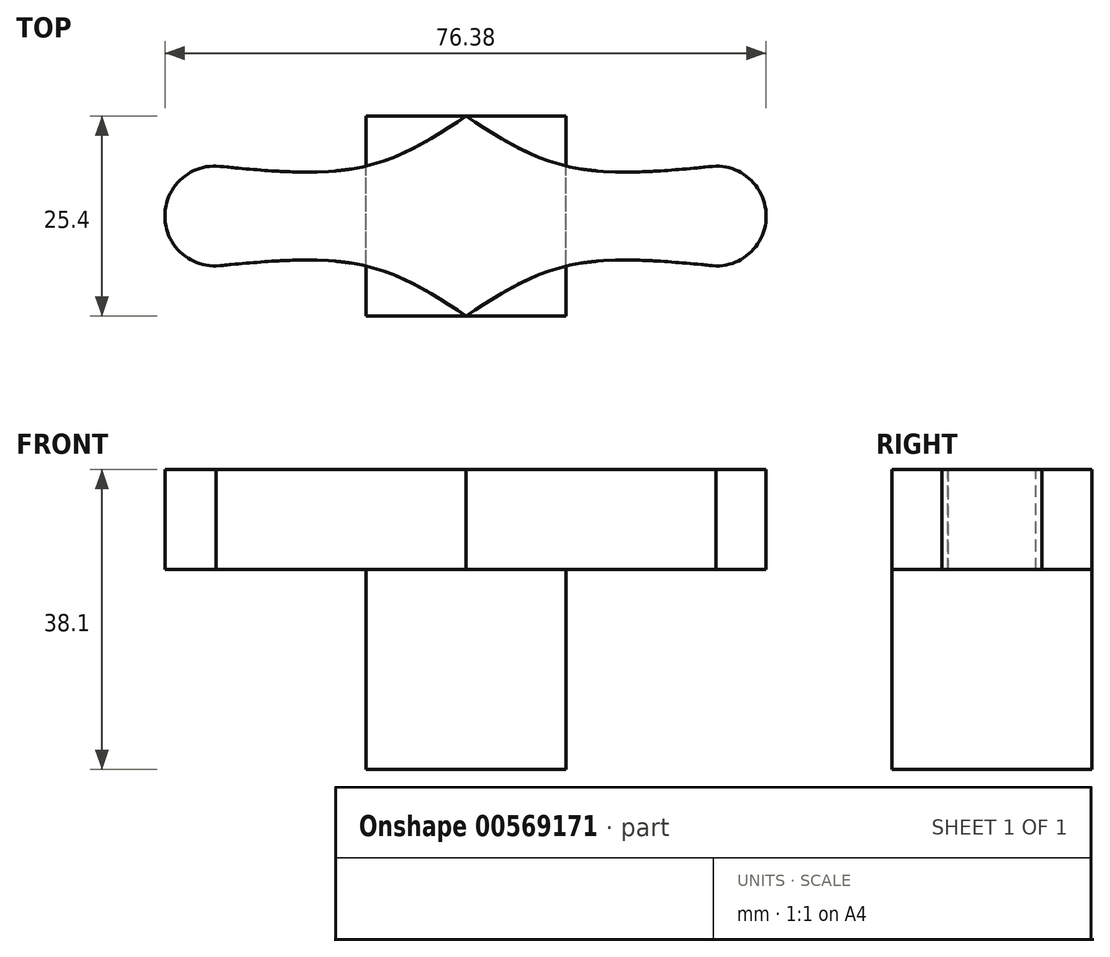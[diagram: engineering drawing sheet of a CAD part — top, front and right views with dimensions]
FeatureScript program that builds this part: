
annotation { "Feature Type Name" : "Feature", "Feature Type Description" : "" }
export const myFeature = defineFeature(function(context is Context, id is Id, definition is map)
    precondition{}
    {
        {
            var Q0;
            Q0=qCreatedBy(makeId("Front.planeOp"),FACE);
            var sketch = newSketch(context, id + "F0", { "sketchPlane" : qUnion([Q0])});
            skLineSegment(sketch, "E0", {"start": v(-11.6, 26.96) * mm, "end": v(-11.6, -11.14) * mm});
            skLineSegment(sketch, "E1", {"start": v(-11.6, -11.14) * mm, "end": v(13.8, -11.14) * mm});
            skLineSegment(sketch, "E2", {"start": v(13.8, -11.14) * mm, "end": v(13.8, 26.96) * mm});
            skLineSegment(sketch, "E3", {"start": v(13.8, 26.96) * mm, "end": v(-11.6, 26.96) * mm});
            skSolve(sketch);
        }
        {
            var Q0;
            Q0=makeQuery(id+"F0.imprint","IMPRINT",FACE,{"disambiguationData":[TD([[makeQuery(id+"F0.imprint","IMPRINT",EDGE,{"derivedFrom":sQuery(id+"F0.wireOp",EDGE,"E0")}),1.0]])]});
            extrude(context, id + "F1", {"entities" : qUnion([Q0]), "depth" : 25.4 * mm, "offsetDistance" : 25.4 * mm});
        }
        {
            var Q0;
            Q0=makeQuery(id+"F1.opExtrude","SWEPT_FACE",FACE,{"disambiguationData":[OSD([sQuery(id+"F0.wireOp",EDGE,"E3")])]});
            var sketch = newSketch(context, id + "F2", { "sketchPlane" : qUnion([Q0])});
            skLineSegment(sketch, "E4", {"start": v(-11.6, -25.4) * mm, "end": v(-11.6, -19.05) * mm});
            skLineSegment(sketch, "E5", {"start": v(-11.6, 0) * mm, "end": v(-11.6, -6.35) * mm});
            skLineSegment(sketch, "E6", {"start": v(13.8, 0) * mm, "end": v(13.8, -6.35) * mm});
            skLineSegment(sketch, "E7", {"start": v(13.8, -6.35) * mm, "end": v(32.85, -6.35) * mm});
            skLineSegment(sketch, "E8", {"start": v(13.8, -25.4) * mm, "end": v(13.8, -19.05) * mm});
            skLineSegment(sketch, "E9", {"start": v(13.8, -19.05) * mm, "end": v(32.86, -19.05) * mm});
            skLineSegment(sketch, "E10", {"start": v(32.86, -19.05) * mm, "end": v(32.85, -6.35) * mm});
            skLineSegment(sketch, "E11", {"start": v(-11.6, -19.05) * mm, "end": v(-30.65, -19.05) * mm});
            skLineSegment(sketch, "E12", {"start": v(-30.65, -19.05) * mm, "end": v(-30.65, -6.35) * mm});
            skLineSegment(sketch, "E13", {"start": v(-30.65, -6.35) * mm, "end": v(-11.6, -6.35) * mm});
            skSolve(sketch);
        }
        {
            var Q0;
            {var subQ0=sQuery(id+"F2.wireOp",EDGE,"E11");Q0=makeQuery(id+"F2.imprint","IMPRINT",FACE,{"disambiguationData":[TD([[makeQuery(id+"F2.imprint","IMPRINT",EDGE,{"derivedFrom":subQ0}),-1.0]])]});}
            var Q1;
            {var subQ0=sQuery(id+"F2.wireOp",EDGE,"E7");Q1=makeQuery(id+"F2.imprint","IMPRINT",FACE,{"disambiguationData":[TD([[makeQuery(id+"F2.imprint","IMPRINT",EDGE,{"derivedFrom":subQ0}),-1.0]])]});}
            extrude(context, id + "F3", {"entities" : qUnion([Q0, Q1]), "operationType" : NewBodyOperationType.ADD, "depth" : -12.7 * mm, "offsetDistance" : 25.4 * mm});
        }
        {
            var Q0;
            {var subQ0=sQuery(id+"F0.wireOp",EDGE,"E3");Q0=makeQuery(id+"F3.boolean.opBoolean","MERGE",FACE,{"derivedFrom":[makeQuery(id+"F1.opExtrude","SWEPT_FACE",FACE,{"disambiguationData":[OSD([subQ0])]}),makeQuery(id+"F3.opExtrude","CAP_FACE",FACE,{"disambiguationData":[OSD([sQuery(id+"F0.wireOp",EDGE,"E2"),subQ0,sQuery(id+"F2.wireOp",EDGE,"E7"),sQuery(id+"F2.wireOp",EDGE,"E9"),sQuery(id+"F2.wireOp",EDGE,"E10")])],"isStart":true}),makeQuery(id+"F3.opExtrude","CAP_FACE",FACE,{"disambiguationData":[OSD([sQuery(id+"F0.wireOp",EDGE,"E0"),subQ0,sQuery(id+"F2.wireOp",EDGE,"E11"),sQuery(id+"F2.wireOp",EDGE,"E12"),sQuery(id+"F2.wireOp",EDGE,"E13")])],"isStart":true})]});}
            var sketch = newSketch(context, id + "F4", { "sketchPlane" : qUnion([Q0])});
            skLineSegment(sketch, "E14", {"start": v(-11.6, -25.4) * mm, "end": v(1.1, -25.4) * mm});
            skFitSpline(sketch, "E15", {"points": [v(1.1, -25.4) * mm, v(-11.6, -19.05) * mm, v(-30.65, -19.05) * mm], "startDerivative": vector(-25.54, 16.88) * mm, "endDerivative": vector(-37.67, -3.68) * mm});
            skLineSegment(sketch, "E16", {"start": v(-11.6, 0) * mm, "end": v(1.1, 0) * mm});
            skFitSpline(sketch, "E17", {"points": [v(1.1, 0) * mm, v(-11.6, -6.35) * mm, v(-30.65, -6.35) * mm], "startDerivative": vector(-25.54, -16.88) * mm, "endDerivative": vector(-37.67, 3.68) * mm});
            skFitSpline(sketch, "E18", {"points": [v(1.1, 0) * mm, v(13.8, -6.35) * mm, v(32.85, -6.35) * mm], "startDerivative": vector(25.54, -16.88) * mm, "endDerivative": vector(37.67, 3.68) * mm});
            skFitSpline(sketch, "E19", {"points": [v(1.1, -25.4) * mm, v(13.8, -19.05) * mm, v(32.86, -19.05) * mm], "startDerivative": vector(25.54, 16.88) * mm, "endDerivative": vector(37.68, -3.68) * mm});
            skSolve(sketch);
        }
        {
            var Q0;
            {var subQ0=sQuery(id+"F4.wireOp",EDGE,"E14");Q0=makeQuery(id+"F4.imprint","IMPRINT",FACE,{"disambiguationData":[TD([[makeQuery(id+"F4.imprint","IMPRINT",EDGE,{"derivedFrom":subQ0}),-1.0]])]});}
            var Q1;
            {var subQ1=sQuery(id+"F2.wireOp",EDGE,"E9");var subQ2=sQuery(id+"F0.wireOp",EDGE,"E3");var subQ3=sQuery(id+"F0.wireOp",EDGE,"E2");var subQ5=makeQuery(id+"F3.boolean.opBoolean","SPLIT",EDGE,{"disambiguationData":[TD([makeQuery(id+"F3.opExtrude","SWEPT_FACE",FACE,{"disambiguationData":[OSD([subQ1])]})])],"derivedFrom":makeQuery(id+"F1.opExtrude","SWEPT_EDGE",EDGE,{"disambiguationData":[OSD([subQ3,subQ2])]})});Q1=makeQuery(id+"F4.imprint","IMPRINT",FACE,{"disambiguationData":[TD([[makeQuery(id+"F4.imprint","IMPRINT",EDGE,{"derivedFrom":subQ5}),1.0]])]});}
            var Q2;
            {var subQ1=sQuery(id+"F2.wireOp",EDGE,"E7");var subQ2=sQuery(id+"F0.wireOp",EDGE,"E3");var subQ3=sQuery(id+"F0.wireOp",EDGE,"E2");var subQ5=makeQuery(id+"F3.boolean.opBoolean","SPLIT",EDGE,{"disambiguationData":[TD([makeQuery(id+"F3.opExtrude","SWEPT_FACE",FACE,{"disambiguationData":[OSD([subQ1])]})])],"derivedFrom":makeQuery(id+"F1.opExtrude","SWEPT_EDGE",EDGE,{"disambiguationData":[OSD([subQ3,subQ2])]})});Q2=makeQuery(id+"F4.imprint","IMPRINT",FACE,{"disambiguationData":[TD([[makeQuery(id+"F4.imprint","IMPRINT",EDGE,{"derivedFrom":subQ5}),1.0]])]});}
            var Q3;
            {var subQ0=sQuery(id+"F4.wireOp",EDGE,"E16");Q3=makeQuery(id+"F4.imprint","IMPRINT",FACE,{"disambiguationData":[TD([[makeQuery(id+"F4.imprint","IMPRINT",EDGE,{"derivedFrom":subQ0}),1.0]])]});}
            var Q4;
            {var subQ2=sQuery(id+"F2.wireOp",EDGE,"E9");var subQ3=makeQuery(id+"F3.opExtrude","CAP_EDGE",EDGE,{"disambiguationData":[OSD([subQ2])],"isStart":true});Q4=makeQuery(id+"F4.imprint","IMPRINT",FACE,{"disambiguationData":[TD([[makeQuery(id+"F4.imprint","IMPRINT",EDGE,{"derivedFrom":subQ3}),1.0]])]});}
            var Q5;
            {var subQ2=sQuery(id+"F2.wireOp",EDGE,"E7");var subQ3=makeQuery(id+"F3.opExtrude","CAP_EDGE",EDGE,{"disambiguationData":[OSD([subQ2])],"isStart":true});Q5=makeQuery(id+"F4.imprint","IMPRINT",FACE,{"disambiguationData":[TD([[makeQuery(id+"F4.imprint","IMPRINT",EDGE,{"derivedFrom":subQ3}),-1.0]])]});}
            var Q6;
            {var subQ1=sQuery(id+"F2.wireOp",EDGE,"E13");var subQ2=makeQuery(id+"F3.opExtrude","CAP_EDGE",EDGE,{"disambiguationData":[OSD([subQ1])],"isStart":true});Q6=makeQuery(id+"F4.imprint","IMPRINT",FACE,{"disambiguationData":[TD([[makeQuery(id+"F4.imprint","IMPRINT",EDGE,{"derivedFrom":subQ2}),-1.0]])]});}
            var Q7;
            {var subQ2=sQuery(id+"F2.wireOp",EDGE,"E11");var subQ3=makeQuery(id+"F3.opExtrude","CAP_EDGE",EDGE,{"disambiguationData":[OSD([subQ2])],"isStart":true});Q7=makeQuery(id+"F4.imprint","IMPRINT",FACE,{"disambiguationData":[TD([[makeQuery(id+"F4.imprint","IMPRINT",EDGE,{"derivedFrom":subQ3}),-1.0]])]});}
            extrude(context, id + "F5", {"entities" : qUnion([Q0, Q1, Q2, Q3, Q4, Q5, Q6, Q7]), "operationType" : NewBodyOperationType.REMOVE, "oppositeDirection" : true, "depth" : 12.7 * mm, "offsetDistance" : 25.4 * mm});
        }
        {
            var Q0;
            {var subQ0=sQuery(id+"F0.wireOp",EDGE,"E3");Q0=makeQuery(id+"F3.boolean.opBoolean","MERGE",FACE,{"derivedFrom":[makeQuery(id+"F1.opExtrude","SWEPT_FACE",FACE,{"disambiguationData":[OSD([subQ0])]}),makeQuery(id+"F3.opExtrude","CAP_FACE",FACE,{"disambiguationData":[OSD([sQuery(id+"F0.wireOp",EDGE,"E2"),subQ0,sQuery(id+"F2.wireOp",EDGE,"E7"),sQuery(id+"F2.wireOp",EDGE,"E9"),sQuery(id+"F2.wireOp",EDGE,"E10")])],"isStart":true}),makeQuery(id+"F3.opExtrude","CAP_FACE",FACE,{"disambiguationData":[OSD([sQuery(id+"F0.wireOp",EDGE,"E0"),subQ0,sQuery(id+"F2.wireOp",EDGE,"E11"),sQuery(id+"F2.wireOp",EDGE,"E12"),sQuery(id+"F2.wireOp",EDGE,"E13")])],"isStart":true})]});}
            var sketch = newSketch(context, id + "F6", { "sketchPlane" : qUnion([Q0])});
            skArc(sketch, "E20", {"start": v(-30.65, -6.35) * mm, "mid": v(-37.17, -12.7) * mm, "end": v(-30.65, -19.05) * mm});
            skArc(sketch, "E21", {"start": v(32.86, -19.05) * mm, "mid": v(39.2, -12.7) * mm, "end": v(32.85, -6.35) * mm});
            skSolve(sketch);
        }
        {
            var Q0;
            Q0=makeQuery(id+"F6.imprint","IMPRINT",FACE,{"disambiguationData":[TD([[makeQuery(id+"F6.imprint","IMPRINT",EDGE,{"derivedFrom":sQuery(id+"F6.wireOp",EDGE,"E21")}),1.0]])]});
            var Q1;
            Q1=makeQuery(id+"F6.imprint","IMPRINT",FACE,{"disambiguationData":[TD([[makeQuery(id+"F6.imprint","IMPRINT",EDGE,{"derivedFrom":sQuery(id+"F6.wireOp",EDGE,"E20")}),1.0]])]});
            extrude(context, id + "F7", {"entities" : qUnion([Q0, Q1]), "operationType" : NewBodyOperationType.ADD, "depth" : -12.7 * mm, "offsetDistance" : 25.4 * mm});
        }
    });
